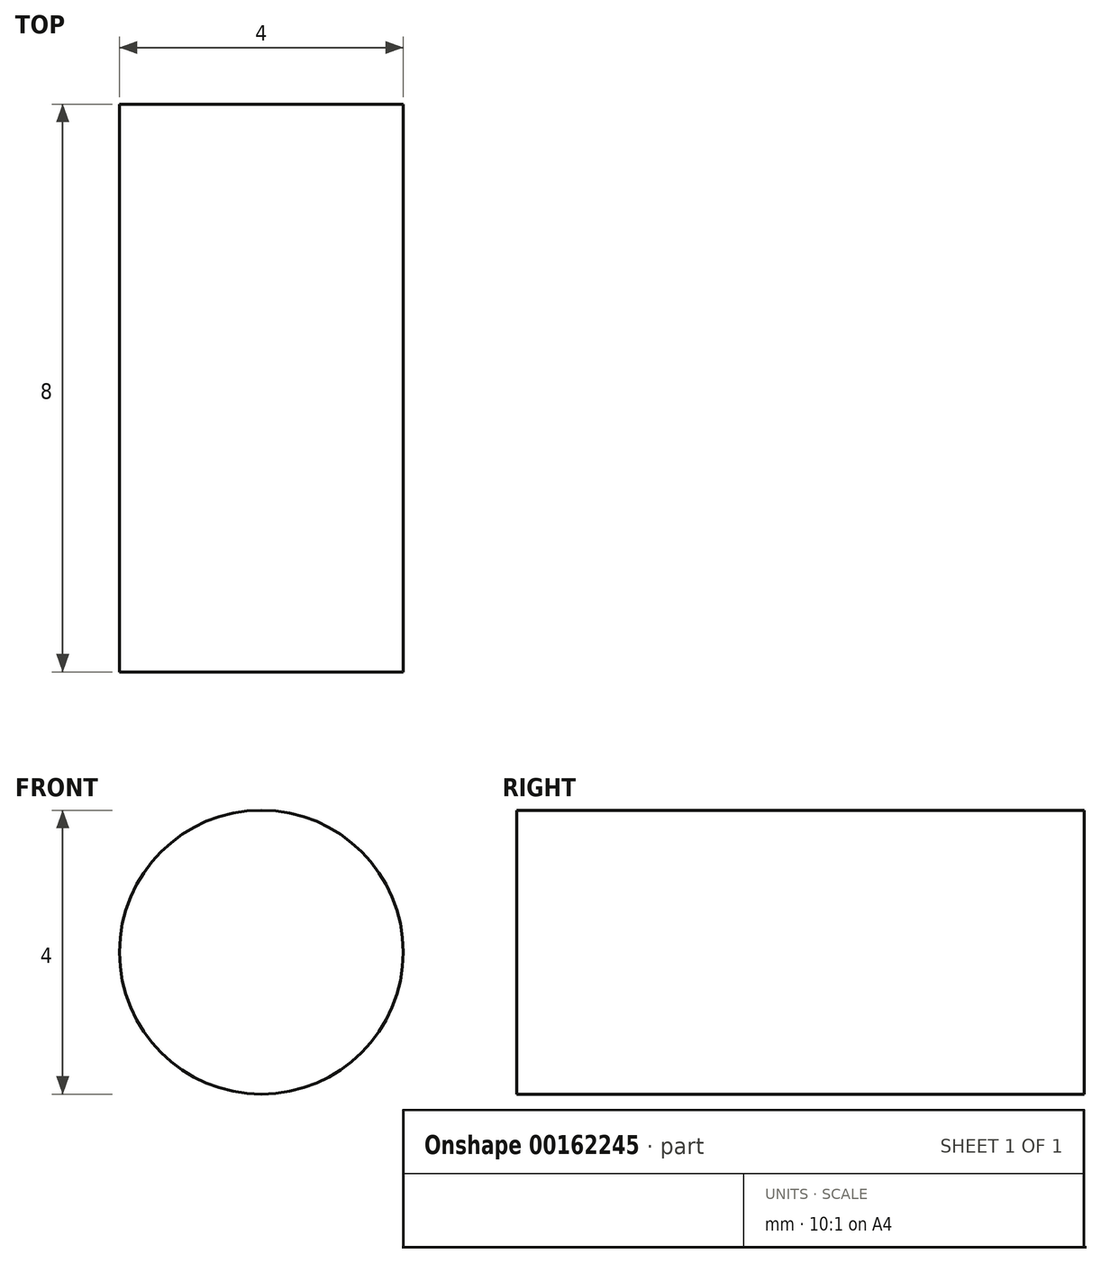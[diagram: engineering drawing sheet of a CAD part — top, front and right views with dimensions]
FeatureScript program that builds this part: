
annotation { "Feature Type Name" : "Feature", "Feature Type Description" : "" }
export const myFeature = defineFeature(function(context is Context, id is Id, definition is map)
    precondition{}
    {
        {
            var Q0;
            Q0=qCreatedBy(makeId("Front.planeOp"),FACE);
            var sketch = newSketch(context, id + "F0", { "sketchPlane" : qUnion([Q0])});
            skCircle(sketch, "E0", {"center": v(0, 0) * mm, "radius": 2 * mm});
            skSolve(sketch);
        }
        {
            var Q0;
            Q0 = qSketchRegion(id + "F0", true);
            extrude(context, id + "F1", {"entities" : qUnion([Q0]), "depth" : 8 * mm});
        }
    });
